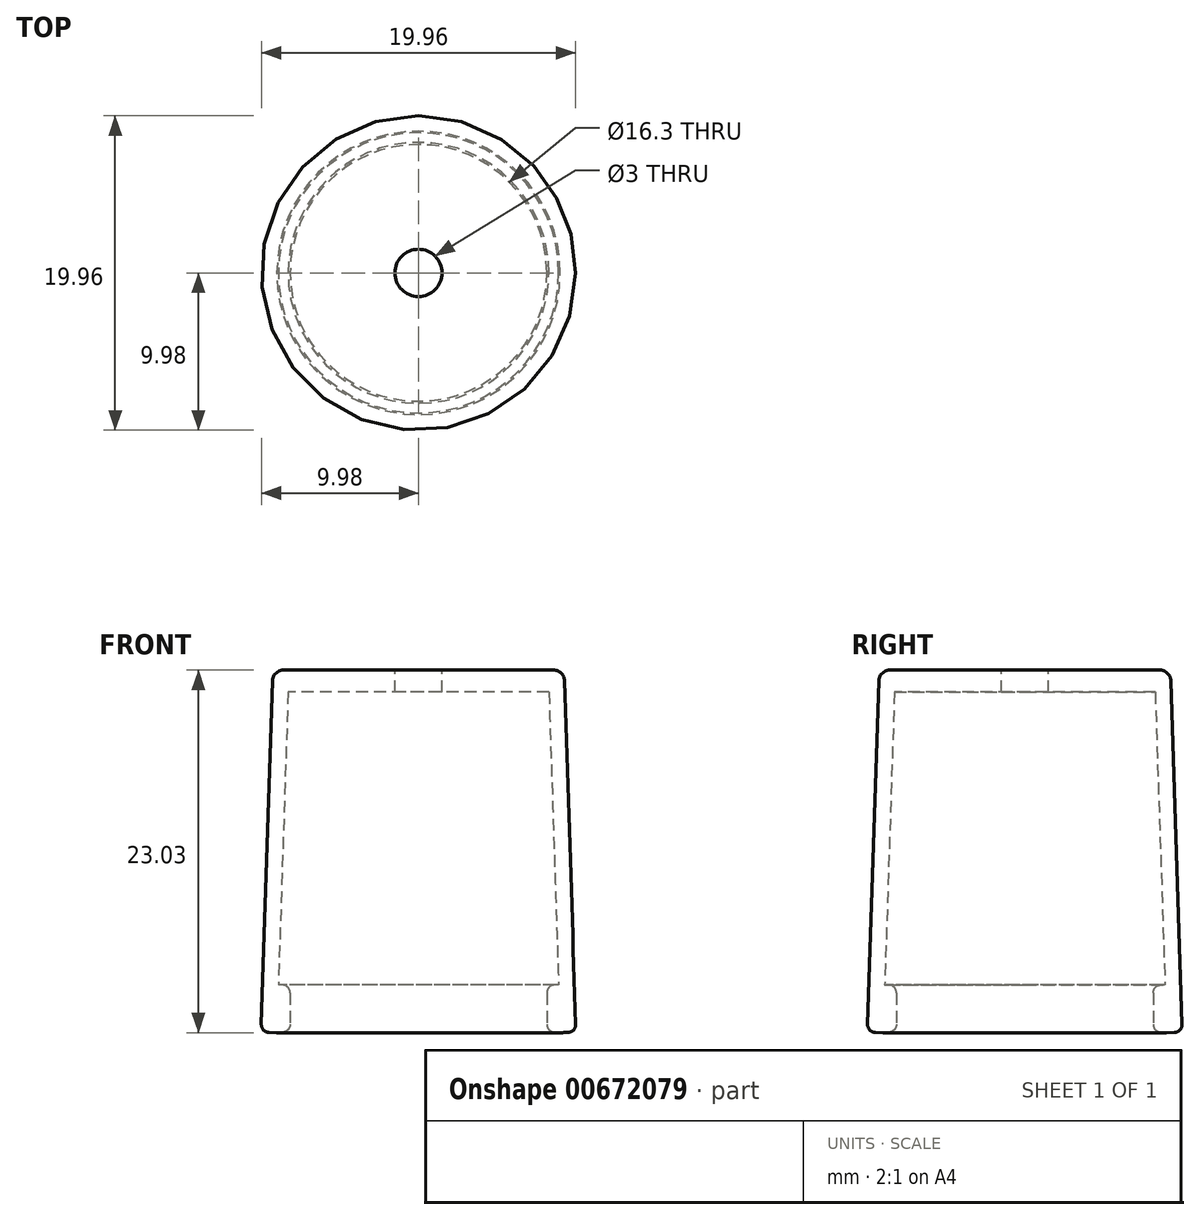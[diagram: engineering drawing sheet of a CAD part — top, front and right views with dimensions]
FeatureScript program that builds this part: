
annotation { "Feature Type Name" : "Feature", "Feature Type Description" : "" }
export const myFeature = defineFeature(function(context is Context, id is Id, definition is map)
    precondition{}
    {
        {
            var Q0;
            Q0=qCreatedBy(makeId("Front.planeOp"),FACE);
            var sketch = newSketch(context, id + "F0", { "sketchPlane" : qUnion([Q0])});
            skLineSegment(sketch, "E0", {"start": v(0, 23) * mm, "end": v(-9.25, 23) * mm});
            skLineSegment(sketch, "E1", {"start": v(-9.25, 23) * mm, "end": v(-10, 0) * mm});
            skLineSegment(sketch, "E2.0", {"start": v(-8.28, 21.6) * mm, "end": v(-9, -0.03) * mm});
            skLineSegment(sketch, "E2.1", {"start": v(0, 21.6) * mm, "end": v(-8.28, 21.6) * mm});
            skLineSegment(sketch, "E3", {"start": v(-10, 0) * mm, "end": v(-9, -0.03) * mm});
            skLineSegment(sketch, "E4", {"start": v(0, 31.13) * mm, "end": v(0, -6) * mm, "construction": true});
            skLineSegment(sketch, "E5", {"start": v(0, 23) * mm, "end": v(0, 21.6) * mm});
            skSolve(sketch);
        }
        {
            var Q0;
            Q0=qCreatedBy(makeId("Top.planeOp"),FACE);
            var sketch = newSketch(context, id + "F1", { "sketchPlane" : qUnion([Q0])});
            skCircle(sketch, "E6", {"center": v(0, 0) * mm, "radius": 9 * mm});
            skCircle(sketch, "E7", {"center": v(0, 0) * mm, "radius": 8.15 * mm});
            skSolve(sketch);
        }
        {
            var Q0;
            Q0 = qSketchRegion(id + "F0", true);
            var Q1;
            Q1=sQuery(id+"F0.wireOp",EDGE,"E4");
            revolve(context, id + "F2", {"entities" : qUnion([Q0]), "axis" : qUnion([Q1]), "revolveType" : RevolveType.FULL});
        }
        {
            var Q0;
            Q0 = qSketchRegion(id + "F0", true);
            var Q1;
            Q1=sQuery(id+"F0.wireOp",EDGE,"E4");
            revolve(context, id + "F3", {"operationType" : NewBodyOperationType.ADD, "entities" : qUnion([Q0]), "axis" : qUnion([Q1]), "revolveType" : RevolveType.FULL});
        }
        {
            var Q0;
            Q0 = qSketchRegion(id + "F1", true);
            extrude(context, id + "F4", {"entities" : qUnion([Q0]), "operationType" : NewBodyOperationType.ADD, "depth" : 3 * mm, "offsetDistance" : 25 * mm});
        }
        {
            var Q0;
            Q0=qCreatedBy(makeId("Top.planeOp"),FACE);
            cPlane(context, id + "F5", {"entities" : qUnion([Q0]), "cplaneType" : CPlaneType.OFFSET, "offset" : 23 * mm, "width" : 150 * mm, "height" : 150 * mm});
        }
        {
            var Q0;
            Q0=qCreatedBy(id+"F5.planeOp",FACE);
            var sketch = newSketch(context, id + "F6", { "sketchPlane" : qUnion([Q0])});
            skPoint(sketch, "E8", {"position": v(0, 0) * mm});
            skSolve(sketch);
        }
        {
            var Q0;
            Q0=sQuery(id+"F6.wireOp",VERTEX,"E8");
            var Q1;
            Q1=makeQuery(id+"F2.opRevolve","SWEPT_BODY",BODY,{"disambiguationData":[OSD([sQuery(id+"F0.wireOp",EDGE,"E0"),sQuery(id+"F0.wireOp",EDGE,"E1"),sQuery(id+"F0.wireOp",EDGE,"E2.0"),sQuery(id+"F0.wireOp",EDGE,"E2.1"),sQuery(id+"F0.wireOp",EDGE,"E3"),sQuery(id+"F0.wireOp",EDGE,"E5")])]});
            hole(context, id + "F7", {"style" : HoleStyle.SIMPLE, "endStyle" : HoleEndStyle.BLIND, "holeDiameter" : 3 * mm, "majorDiameter" : 5 * mm, "holeDepth" : 12 * mm, "isTappedThrough" : true, "tappedDepth" : 12 * mm, "tapClearance" : 3, "startFromSketch" : true, "locations" : qUnion([Q0]), "scope" : qUnion([Q1])});
        }
        {
            var Q0;
            Q0=makeQuery(id+"F2.opRevolve","SWEPT_EDGE",EDGE,{"disambiguationData":[OSD([sQuery(id+"F0.wireOp",EDGE,"E0"),sQuery(id+"F0.wireOp",EDGE,"E1")])]});
            fillet(context, id + "F8", {"entities" : qUnion([Q0]), "radius" : 0.7 * mm, "tangentPropagation" : true, "allowEdgeOverflow" : false});
        }
        {
            var Q0;
            Q0=makeQuery(id+"F2.opRevolve","SWEPT_EDGE",EDGE,{"disambiguationData":[OSD([sQuery(id+"F0.wireOp",EDGE,"E1"),sQuery(id+"F0.wireOp",EDGE,"E3")])]});
            var Q1;
            Q1=makeQuery(id+"F4.opExtrude","CAP_EDGE",EDGE,{"disambiguationData":[OSD([sQuery(id+"F1.wireOp",EDGE,"E7")])],"isStart":true});
            var Q2;
            Q2=makeQuery(id+"F4.opExtrude","CAP_EDGE",EDGE,{"disambiguationData":[OSD([sQuery(id+"F1.wireOp",EDGE,"E7")])],"isStart":false});
            var Q3;
            Q3=makeQuery(id+"F7.hole-0.boolean.opBoolean","COPY",EDGE,{"derivedFrom":makeQuery(id+"F7.hole-0.opRevolve","SWEPT_EDGE",EDGE,{"disambiguationData":[OSD([sQuery(id+"F7.hole-0.sketch.wireOp",EDGE,"core_line_2"),sQuery(id+"F7.hole-0.sketch.wireOp",EDGE,"core_line_3")])]})});
            var Q4;
            Q4=makeQuery(id+"F7.hole-0.boolean.opBoolean","INTERSECT",EDGE,{"derivedFrom":[makeQuery(id+"F2.opRevolve","SWEPT_FACE",FACE,{"disambiguationData":[OSD([sQuery(id+"F0.wireOp",EDGE,"E2.1")])]}),makeQuery(id+"F7.hole-0.opRevolve","SWEPT_FACE",FACE,{"disambiguationData":[OSD([sQuery(id+"F7.hole-0.sketch.wireOp",EDGE,"core_line_2")])]})]});
            fillet(context, id + "F9", {"entities" : qUnion([Q0, Q1, Q2, Q3, Q4]), "radius" : 0.5 * mm, "tangentPropagation" : true, "allowEdgeOverflow" : false});
        }
    });
